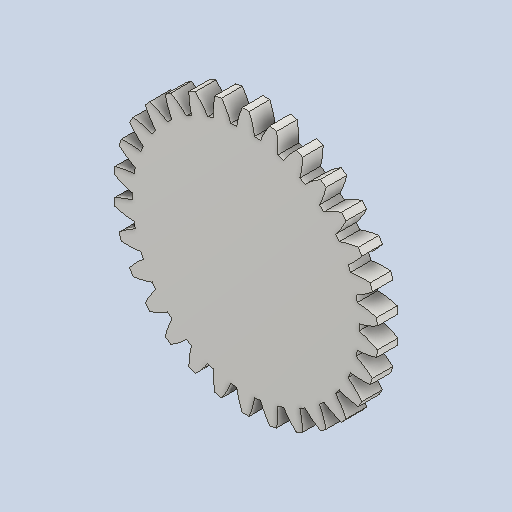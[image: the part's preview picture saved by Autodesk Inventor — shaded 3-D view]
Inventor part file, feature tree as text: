
AUTODESK INVENTOR PART (.ipt)
format: ipt  version: 2023 (Build 270158000, 158)  size: 258,560 bytes
history: native  units: mm (DEFAULTED — no unit token found)
features: plane x3, other x3, sketch x2, extrude x1
ambient origin geometry x8: Origin, YZ Plane, XZ Plane, XY Plane, X Axis, Y Axis, Z Axis, Center Point
bodies: Solid1 (feature_tree)
feature tree (9):
  extrude  "Extrusion1"  Depth=5.0mm TaperAngle=0.0deg
  plane  "Work Plane2"
  plane  "Work Plane8"
  plane  "Work Plane9"
  other  "Spur Gear"
  sketch  "Sketch1"  dims[d0=64.0mm d1=5.0mm d2=0.0mm]
  sketch  "Sketch2"  dims[d3=60.0mm d4=10.0mm d5=0.0mm d16=40.0mm d17=0.0mm d34=1.047198mm d39=0.0mm d41=0.0mm d43=40.0mm d46=40.0mm d47=0.0mm d48=0.0mm]
  other  "Srf1"
  other  "Pitch Diameter"
